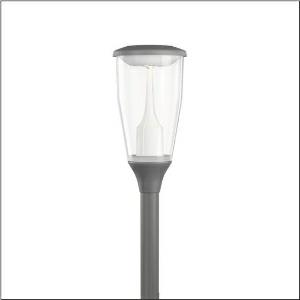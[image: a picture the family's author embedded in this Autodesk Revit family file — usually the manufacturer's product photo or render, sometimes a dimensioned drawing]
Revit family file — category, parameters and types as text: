
# Revit family: dl_11_iq___st1_2a_5xa5565mf14h000022_0c06
name_source: partatom
category: Lighting Fixtures
units: mm (PartAtom-declared; Revit-internal decimal feet)

## family parameters
Cut with Voids When Loaded = No
Host = Face
Light Source = No
Part Type = Normal
Room Calculation Point = No
Round Connector Dimension = Use Diameter
Shared = No

## types (1)
- --- (1 x LED, 1560 lm, 11.8 W, 2700K)
    Apparent Load = 12 VA
    CIE Flux Codes = 24 63 94 96 100
    Color Rendering = 70
    Color Temperature = 2700K
    Default Elevation = 1800 mm
    Description = DL 11 iQ, mast luminaire, Module 540 iQ-SR, primary light control with 3 zone facetted reflector, of plastic, silver coated, highly specular, structured, primary optical cover: cover, of PMMA, transparent, light distribution: ST1.2a, light emission: direct distribution, primary light characteristic: asymmetric, installation type: post-top, LED, High Power LED, rated luminous flux: 1.560lm, luminous efficacy: 149lm/W, light colour: 727, colour temperature: 2700K, control gear: iQ Street-Remote, control: Street-Remote, Auto-Match, Temp-Guard, Lumen-Switch, Night-Set, Smart-Wire, Light-Fading, Desk-Remote (wireless, voltage-free reading and setting of iQ features in the workshop via application-optimized NFC function/RFID function), optimised constant luminous flux control (CLO 2.0), mains connection: 220..240V, AC, 50/60Hz, connection cable pre-assembled, cable length: 5,5m, start of lifetime: 12W, end of service life: 12W, reduction: 5W, luminaire housing, upper part, of diecast aluminium, coated, SITECO metallic grey (DB 702S), spigot size: 60mm (post-top), mounting height: 3..5m, post-top mast mounting element, of diecast aluminium, coated, SITECO metallic grey (DB 702S), Module 540 iQ-SR, traffic white (RAL 9016), equipment: standard, protection rating (complete): IP66, insulation class (complete): insulation class II (safety insulation), certification: CE, ENEC, ENEC+, VDE, impact resistance: IK07, packaging unit: 1 piece

Light Distribution: ST1.2a
    Height = 665 mm
    Lamp = 1 x LED
    Lamp Light Flux = 1560 lm
    Lamp Power = 11.8 W
    Lamp count = 1
    Length = 334 mm
    Luminous efficacy = 132 lm/W
    Manufacturer = Siteco
    ModVariant = No
    Model = 5XA5565MF14H000022
    Number of Poles = 1
    OnlyDefault = Yes
    Power Factor = 1
    Product Name = DL 11 iQ | ST1.2a
    Product group = mast luminaire | pylon top
    ProductGroupID = 6100
    Protection Class = Protection class II
    Protection Degree = IP 66
    RLX_Detail_Level = 1
    RLX_Emergency_Light_Flux = 0 lm
    RLX_Emergency_Type = 0
    RLX_Emergency_Type_DB = No
    RlxData = <blob elided: 153177 chars, md5=051ff20b>
    Socket = socket
    Standby Power = 0 W
    System Light Flux = 1560 lm
    System Power = 12 W
    Type Comments = factory setting: luminous flux: 100 % | dim-lin: 254 | 472 mA
    Type Image = l_1258354.jpg
    URL = http://relux.com
    VarID = @adj_099033
    Voltage = 0 V
    Weight = 0.00 kg
    Width = 0 mm  [stored 0 ft]

note: [stored X ft] marks values corroborated as IEEE doubles in the binary element streams (Revit-internal decimal feet)

## geometry (parser evidence)
native form markers: Blend x4, Sweep x12
no freeform markers — native parametric forms only
